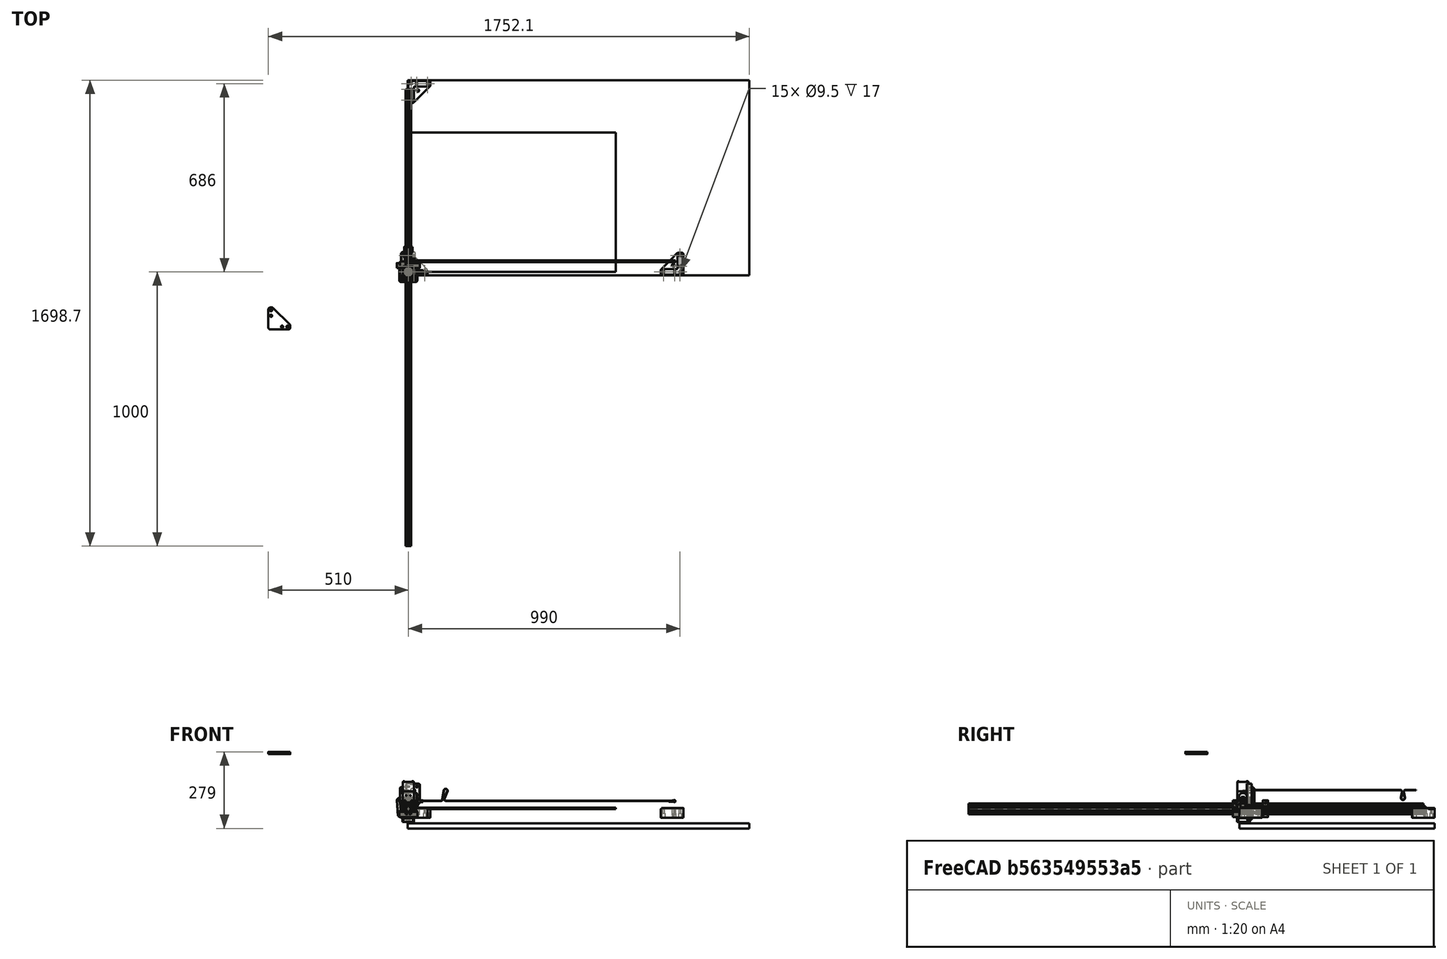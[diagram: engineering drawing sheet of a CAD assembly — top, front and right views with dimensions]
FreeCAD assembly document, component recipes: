
FREECAD ASSEMBLY — COMPONENT RECIPES ("laser-cnc-wf")

This assembly document has 18 components, labeled P0..P17 below (a component is one placed body or linked part). 17 of them carry a construction recipe — the FreeCAD feature program that regenerates the part from scratch, quoted from this document or its linked companion documents; the rest are supplied as boundary geometry only. No exploded tour is included for this assembly.
COMPONENT P0 — recipe-attached ("VSlotBearing", modeled in this document).
Construction recipe (the document's own serialized feature program — sketch geometry with constraints, then the solid features built on it; lengths are millimeters unless a unit is written):

FEATURE [Sketcher::SketchObject] Sketch002  label="BearingProfile"
  FullyConstrained = true
  MapMode = 5
  Placement = pos=(0,0,0) rot=(1,0,0;1.5708rad)
  Support = -> [XZ_Plane001]
  sketch-geometry (9):
    g0: LineSegment StartX=-5.085 StartY=9.91981 StartZ=0 EndX=-5.085 EndY=2.5 EndZ=0
    g1: LineSegment StartX=5.085 StartY=9.91981 StartZ=0 EndX=5.085 EndY=2.5 EndZ=0
    g2: LineSegment StartX=-5.085 StartY=2.5 StartZ=0 EndX=5.085 EndY=2.5 EndZ=0
    g3: LineSegment StartX=-2.98481 StartY=12.02 StartZ=0 EndX=2.98481 EndY=12.02 EndZ=0
    g4: LineSegment StartX=-5.085 StartY=9.91981 StartZ=0 EndX=-2.98481 EndY=12.02 EndZ=0
    g5: LineSegment StartX=2.98481 StartY=12.02 StartZ=0 EndX=5.085 EndY=9.91981 EndZ=0
    g6: GeomPoint X=-7.5024 Y=7.5024 Z=0
    g7: GeomPoint X=7.5024 Y=-7.5024 Z=0
    g8: LineSegment StartX=-7.5024 StartY=7.5024 StartZ=0 EndX=7.5024 EndY=-7.5024 EndZ=0
  constraints (23):
    c: Vertical(g0)
    c: Vertical(g1)
    c: Symmetric(g0,g1,g-2)
    c: DistanceX(g0,g1) = 10.17  'Width'
    c: DistanceY(g-1,g0) = 2.5
    c: Coincident(g2,g0)
    c: Coincident(g2,g1)
    c: Horizontal(g2)
    c: Horizontal(g3)
    c: DistanceY(g3) = 12.02
    c: Coincident(g4,g0)
    c: Coincident(g4,g3)
    c: Coincident(g5,g3)
    c: Coincident(g5,g1)
    c: Angle(g5,g-1) = 0.785398
    c: Perpendicular(g5,g4)
    c: DistanceY(g0) = 9.91981
    c: PointOnObject(g6,g4)
    c: Symmetric(g7,g6,g-1)
    c: Coincident(g8,g6)
    c: Coincident(g8,g7)
    c: Perpendicular(g4,g8)
    c: Distance(g8) = 21.22
FEATURE [PartDesign::Revolution] Revolution
  Angle = 360
  Axis = (1,0,0)
  Base = (0,0,0)
  Placement = pos=(0,0,0) rot=(1,0,0;1.5708rad)
  Profile = -> Sketch002
  ReferenceAxis = -> Sketch002 [H_Axis]
FEATURE [PartDesign::Body] Body  label="VSlotBearing"
  Group = -> [Sketch002,Revolution]
  Origin = -> Origin001
  Tip = -> Revolution
COMPONENT P1 — recipe-attached ("Brace", modeled in this document).
Construction recipe (the document's own serialized feature program — sketch geometry with constraints, then the solid features built on it; lengths are millimeters unless a unit is written):

FEATURE [Sketcher::SketchObject] Sketch006  label="BraceProfile"
  FullyConstrained = true
  MapMode = 5
  Support = -> [XY_Plane009]
  sketch-geometry (20):
    g0: LineSegment StartX=-10 StartY=63 StartZ=0 EndX=-10 EndY=-3 EndZ=0
    g1: LineSegment StartX=-3 StartY=-10 StartZ=0 EndX=63 EndY=-10 EndZ=0
    g2: LineSegment StartX=70 StartY=-3 StartZ=0 EndX=70 EndY=3 EndZ=0
    g3: LineSegment StartX=67.9497 StartY=7.94975 StartZ=0 EndX=7.94975 EndY=67.9497 EndZ=0
    g4: LineSegment StartX=3 StartY=70 StartZ=0 EndX=-3 EndY=70 EndZ=0
    g5: Circle CenterX=40 CenterY=0 CenterZ=0 NormalX=0 NormalY=0 NormalZ=1 AngleXU=0 Radius=4
    g6: Circle CenterX=60 CenterY=0 CenterZ=0 NormalX=0 NormalY=0 NormalZ=1 AngleXU=0 Radius=4
    g7: Circle CenterX=0 CenterY=40 CenterZ=0 NormalX=0 NormalY=0 NormalZ=1 AngleXU=0 Radius=4
    g8: Circle CenterX=0 CenterY=60 CenterZ=0 NormalX=0 NormalY=0 NormalZ=1 AngleXU=0 Radius=4
    g9: LineSegment StartX=10 StartY=100 StartZ=0 EndX=10 EndY=-10 EndZ=0
    g10: LineSegment StartX=10 StartY=-10 StartZ=0 EndX=-10 EndY=-10 EndZ=0
    g11: LineSegment StartX=-10 StartY=-10 StartZ=0 EndX=-10 EndY=100 EndZ=0
    g12: LineSegment StartX=10 StartY=10 StartZ=0 EndX=160 EndY=10 EndZ=0
    g13: LineSegment StartX=160 StartY=-10 StartZ=0 EndX=10 EndY=-10 EndZ=0
    g14: LineSegment StartX=10 StartY=-10 StartZ=0 EndX=10 EndY=10 EndZ=0
    g15: ArcOfCircle CenterX=-3 CenterY=-3 CenterZ=0 NormalX=0 NormalY=0 NormalZ=1 AngleXU=0 Radius=7 StartAngle=3.14159 EndAngle=4.71239
    g16: ArcOfCircle CenterX=-3 CenterY=63 CenterZ=0 NormalX=0 NormalY=0 NormalZ=1 AngleXU=0 Radius=7 StartAngle=1.5708 EndAngle=3.14159
    g17: ArcOfCircle CenterX=3 CenterY=63 CenterZ=0 NormalX=0 NormalY=0 NormalZ=1 AngleXU=0 Radius=7 StartAngle=0.785398 EndAngle=1.5708
    g18: ArcOfCircle CenterX=63 CenterY=3 CenterZ=0 NormalX=0 NormalY=0 NormalZ=1 AngleXU=0 Radius=7 StartAngle=0 EndAngle=0.785398
    g19: ArcOfCircle CenterX=63 CenterY=-3 CenterZ=0 NormalX=0 NormalY=0 NormalZ=1 AngleXU=0 Radius=7 StartAngle=4.71239 EndAngle=6.28319
  constraints (53):
    c: Vertical(g0)
    c: Horizontal(g1)
    c: Vertical(g2)
    c: Horizontal(g4)
    c: PointOnObject(g5,g-1)
    c: PointOnObject(g6,g-1)
    c: PointOnObject(g7,g-2)
    c: PointOnObject(g8,g-2)
    c: Radius(g7) = 4
    c: Equal(g8,g7)
    c: Equal(g7,g5)
    c: Equal(g5,g6)
    c: Distance(g5,g6) = 20
    c: Distance(g7,g8) = 20
    c: Coincident(g9,g10)
    c: Coincident(g10,g11)
    c: Vertical(g9)
    c: Vertical(g11)
    c: DistanceY(g10,g-1) = 10
    c: DistanceX(g10,g10) = 20
    c: Symmetric(g10,g9,g-2)
    c: DistanceY(g11,g11) = 110
    c: Equal(g9,g11)
    c: Coincident(g13,g14)
    c: Coincident(g14,g12)
    c: Horizontal(g12)
    c: Horizontal(g13)
    c: Vertical(g14)
    c: PointOnObject(g13,g10)
    c: DistanceX(g13,g13) = 150
    c: Equal(g13,g12)
    c: Symmetric(g12,g9,g-1)
    c: DistanceX(g-1,g5) = 40
    c: DistanceY(g-1,g7) = 40
    c: Tangent(g0,g15) = -1.5708
    c: Tangent(g1,g15) = -1.5708
    c: Tangent(g0,g16) = -1.5708
    c: Tangent(g4,g16) = -1.5708
    c: Tangent(g4,g17) = -1.5708
    c: Tangent(g3,g17) = -1.5708
    c: Tangent(g3,g18) = -1.5708
    c: Tangent(g2,g18) = -1.5708
    c: Tangent(g2,g19) = -1.5708
    c: Tangent(g1,g19) = -1.5708
    c: Equal(g18,g15)
    c: Equal(g15,g16)
    c: PointOnObject(g0,g11)
    c: Radius(g16) = 7
    c: DistanceY(g8,g4) = 10
    c: PointOnObject(g1,g13)
    c: DistanceX(g6,g2) = 10
    c: Symmetric(g17,g16,g-2)
    c: Symmetric(g18,g19,g-1)
FEATURE [PartDesign::Pad] Pad002
  Direction = (0,0,1)
  Length = 8
  Length2 = 100
  Profile = -> Sketch006
  Type = 0
FEATURE [PartDesign::Body] Body005  label="Brace"
  Group = -> [Sketch006,Pad002]
  Origin = -> Origin009
  Placement = pos=(-500,-200,200) rot=(0,0,1;0rad)
  Tip = -> Pad002
COMPONENT P2 — recipe-attached ("BoltM5_20", modeled in this document).
Construction recipe (the document's own serialized feature program — sketch geometry with constraints, then the solid features built on it; lengths are millimeters unless a unit is written):

FEATURE [Sketcher::SketchObject] Sketch015
  FullyConstrained = true
  MapMode = 5
  Support = -> [XY_Plane014]
  sketch-geometry (6):
    g0: LineSegment StartX=4.17 StartY=5 StartZ=0 EndX=4.17 EndY=0 EndZ=0
    g1: LineSegment StartX=4.17 StartY=0 StartZ=0 EndX=2.45 EndY=0 EndZ=0
    g2: LineSegment StartX=2.45 StartY=0 StartZ=0 EndX=2.45 EndY=-20 EndZ=0
    g3: LineSegment StartX=2.45 StartY=-20 StartZ=0 EndX=0 EndY=-20 EndZ=0
    g4: LineSegment StartX=4.17 StartY=5 StartZ=0 EndX=0 EndY=5 EndZ=0
    g5: LineSegment StartX=0 StartY=5 StartZ=0 EndX=0 EndY=-20 EndZ=0
  constraints (18):
    c: Coincident(g0,g1)
    c: Horizontal(g1)
    c: Vertical(g0)
    c: PointOnObject(g0,g-1)
    c: Coincident(g2,g3)
    c: Horizontal(g3)
    c: Vertical(g2)
    c: Coincident(g2,g1)
    c: PointOnObject(g3,g-2)
    c: Coincident(g4,g0)
    c: PointOnObject(g4,g-2)
    c: Horizontal(g4)
    c: Coincident(g5,g4)
    c: Coincident(g5,g3)
    c: DistanceX(g4,g4) = 4.17
    c: DistanceY(g0,g0) = 5
    c: DistanceY(g2,g2) = 20
    c: DistanceX(g3,g3) = 2.45
FEATURE [PartDesign::Revolution] Revolution001
  Angle = 360
  Axis = (0,1,0)
  Base = (0,0,0)
  Profile = -> Sketch015
  ReferenceAxis = -> Sketch015 [V_Axis]
FEATURE [PartDesign::Body] Body008  label="BoltM5_20"
  Group = -> [Sketch015,Revolution001]
  Origin = -> Origin014
  Tip = -> Revolution001
COMPONENT P3 — recipe-attached ("Stepper47", modeled in this document).
Construction recipe (the document's own serialized feature program — sketch geometry with constraints, then the solid features built on it; lengths are millimeters unless a unit is written):

FEATURE [Sketcher::SketchObject] Sketch017  label="StepperBodyShape"
  FullyConstrained = true
  MapMode = 5
  Support = -> [XY_Plane015]
  sketch-geometry (8):
    g0: LineSegment StartX=-17.1131 StartY=21 StartZ=0 EndX=17.1131 EndY=21 EndZ=0
    g1: LineSegment StartX=21 StartY=17.1131 StartZ=0 EndX=21 EndY=-17.1131 EndZ=0
    g2: LineSegment StartX=17.1131 StartY=-21 StartZ=0 EndX=-17.1131 EndY=-21 EndZ=0
    g3: LineSegment StartX=-21 StartY=-17.1131 StartZ=0 EndX=-21 EndY=17.1131 EndZ=0
    g4: LineSegment StartX=-21 StartY=17.1131 StartZ=0 EndX=-17.1131 EndY=21 EndZ=0
    g5: LineSegment StartX=17.1131 StartY=21 StartZ=0 EndX=21 EndY=17.1131 EndZ=0
    g6: LineSegment StartX=21 StartY=-17.1131 StartZ=0 EndX=17.1131 EndY=-21 EndZ=0
    g7: LineSegment StartX=-21 StartY=-17.1131 StartZ=0 EndX=-17.1131 EndY=-21 EndZ=0
  constraints (24):
    c: Horizontal(g0)
    c: Horizontal(g2)
    c: Vertical(g1)
    c: Vertical(g3)
    c: Coincident(g7,g3)
    c: Coincident(g7,g2)
    c: Coincident(g6,g2)
    c: Coincident(g6,g1)
    c: Coincident(g5,g1)
    c: Coincident(g5,g0)
    c: Coincident(g4,g0)
    c: Coincident(g4,g3)
    c: Angle(g3,g4) = 2.35619
    c: Parallel(g4,g6)
    c: Perpendicular(g4,g7)
    c: Equal(g4,g5)
    c: Equal(g5,g6)
    c: Equal(g6,g7)
    c: Equal(g3,g0)
    c: Equal(g0,g1)
    c: DistanceX(g3,g1) = 42  'Width'
    c: Symmetric(g0,g2,g-1)
    c: Distance(g0,g1) = 53.9
    c: DistanceY(g-1,g0) = 21  'CenterToEdge'
FEATURE [PartDesign::Pad] Pad007  label="StepperBodyPad"
  Direction = (0,0,1)
  Length = 47.9
  Length2 = 100
  Profile = -> Sketch017
  Reversed = true
  Type = 0
FEATURE [Sketcher::SketchObject] Sketch018
  AttachmentOffset = pos=(0,0,21.1) rot=(0,0,1;0rad)
  FullyConstrained = true
  MapMode = 5
  Placement = pos=(0,0,21.1) rot=(0,0,1;0rad)
  Support = -> [XY_Plane015]
  expr: .AttachmentOffset.Base.z = 69mm - Pad007.Length
  sketch-geometry (3):
    g0: ArcOfCircle CenterX=0 CenterY=0 CenterZ=0 NormalX=0 NormalY=0 NormalZ=1 AngleXU=0 Radius=2.5 StartAngle=2.2143 EndAngle=7.21048
    g1: LineSegment StartX=-1.5 StartY=2 StartZ=0 EndX=1.5 EndY=2 EndZ=0
    g2: LineSegment StartX=1.1641e-12 StartY=2 StartZ=0 EndX=-1.6132e-12 EndY=-2.5 EndZ=0
  constraints (10):
    c: Coincident(g0,g-1)
    c: Coincident(g1,g0)
    c: Coincident(g1,g0)
    c: Radius(g0) = 2.5
    c: PointOnObject(g2,g1)
    c: PointOnObject(g2,g0)
    c: Perpendicular(g1,g2)
    c: PointOnObject(g0,g2)
    c: Distance(g2) = 4.5
    c: Horizontal(g1)
FEATURE [Sketcher::SketchObject] Sketch019
  AttachmentOffset = pos=(0,0,7) rot=(0,0,1;0rad)
  FullyConstrained = true
  MapMode = 5
  Placement = pos=(0,0,7) rot=(0,0,1;0rad)
  Support = -> [XY_Plane015]
  sketch-geometry (1):
    g0: Circle CenterX=0 CenterY=0 CenterZ=0 NormalX=0 NormalY=0 NormalZ=1 AngleXU=0 Radius=4
  constraints (2):
    c: Coincident(g0,g-1)
    c: Radius(g0) = 4
FEATURE [Sketcher::SketchObject] Sketch020
  AttachmentOffset = pos=(0,0,6) rot=(0,0,1;0rad)
  FullyConstrained = true
  MapMode = 5
  Placement = pos=(0,0,6) rot=(0,0,1;0rad)
  Support = -> [XY_Plane015]
  sketch-geometry (12):
    g0: ArcOfCircle CenterX=-15.521 CenterY=-15.521 CenterZ=0 NormalX=0 NormalY=0 NormalZ=1 AngleXU=0 Radius=3.87 StartAngle=3.05556 EndAngle=4.79842
    g1: ArcOfCircle CenterX=15.521 CenterY=15.521 CenterZ=0 NormalX=0 NormalY=0 NormalZ=1 AngleXU=0 Radius=3.87 StartAngle=6.19716 EndAngle=7.94001
    g2: ArcOfCircle CenterX=0 CenterY=0 CenterZ=0 NormalX=0 NormalY=0 NormalZ=1 AngleXU=0 Radius=18 StartAngle=1.65682 EndAngle=3.05556
    g3: ArcOfCircle CenterX=0 CenterY=0 CenterZ=0 NormalX=0 NormalY=0 NormalZ=1 AngleXU=0 Radius=18 StartAngle=4.79842 EndAngle=6.19716
    g4: LineSegment StartX=-12.7279 StartY=12.7279 StartZ=0 EndX=12.7279 EndY=-12.7279 EndZ=0
    g5: LineSegment StartX=-17.9334 StartY=1.5466 StartZ=0 EndX=-19.3767 EndY=-15.1885 EndZ=0
    g6: LineSegment StartX=-15.1885 StartY=-19.3767 StartZ=0 EndX=1.5466 EndY=-17.9334 EndZ=0
    g7: LineSegment StartX=17.9334 StartY=-1.5466 StartZ=0 EndX=19.3767 EndY=15.1885 EndZ=0
    g8: LineSegment StartX=15.1885 StartY=19.3767 StartZ=0 EndX=-1.5466 EndY=17.9334 EndZ=0
    g9: Circle CenterX=-15.521 CenterY=-15.521 CenterZ=0 NormalX=0 NormalY=0 NormalZ=1 AngleXU=0 Radius=1.25
    g10: Circle CenterX=15.521 CenterY=15.521 CenterZ=0 NormalX=0 NormalY=0 NormalZ=1 AngleXU=0 Radius=1.25
    g11: LineSegment StartX=-18.2575 StartY=-18.2575 StartZ=0 EndX=18.2575 EndY=18.2575 EndZ=0
  constraints (28):
    c: Coincident(g2,g-1)
    c: Coincident(g3,g2)
    c: PointOnObject(g4,g2)
    c: PointOnObject(g4,g3)
    c: Symmetric(g4,g4,g2)
    c: Distance(g4) = 36
    c: Coincident(g9,g0)
    c: Coincident(g10,g1)
    c: Equal(g10,g9)
    c: Diameter(g9) = 2.5
    c: Distance(g0,g1) = 43.9
    c: Tangent(g5,g2) = -1.5708
    c: Tangent(g8,g2) = -1.5708
    c: Tangent(g8,g1) = -1.5708
    c: Tangent(g7,g1) = -1.5708
    c: Tangent(g7,g3) = -1.5708
    c: Tangent(g6,g3) = -1.5708
    c: Tangent(g6,g0) = -1.5708
    c: Tangent(g5,g0) = -1.5708
    c: Equal(g0,g1)
    c: Symmetric(g0,g1,g2)
    c: PointOnObject(g11,g0)
    c: PointOnObject(g11,g1)
    c: PointOnObject(g2,g11)
    c: Perpendicular(g11,g4)
    c: Distance(g11) = 51.64
    c: Angle(g11,g-1) = 2.35619
    c: PointOnObject(g0,g11)
FEATURE [Sketcher::SketchObject] Sketch021
  FullyConstrained = true
  MapMode = 5
  Support = -> [XY_Plane015]
  sketch-geometry (1):
    g0: Circle CenterX=0 CenterY=0 CenterZ=0 NormalX=0 NormalY=0 NormalZ=1 AngleXU=0 Radius=17
  constraints (2):
    c: Coincident(g0,g-1)
    c: Diameter(g0) = 34
FEATURE [PartDesign::Pad] Pad010
  BaseFeature = -> Pad007
  Direction = (0,0,1)
  Length = 5
  Length2 = 100
  Profile = -> Sketch021
  Type = 0
FEATURE [PartDesign::Pad] Pad009
  BaseFeature = -> Pad010
  Direction = (0,0,1)
  Length = 1
  Length2 = 100
  Profile = -> Sketch020
  Reversed = true
  Type = 0
FEATURE [PartDesign::Pocket] Pocket006
  BaseFeature = -> Pad009
  Length = 10
  Length2 = 100
  Profile = -> Sketch019
  Type = 0
FEATURE [PartDesign::Pad] Pad008
  BaseFeature = -> Pocket006
  Direction = (0,0,-1)
  Length = 10
  Length2 = 100
  Profile = -> Sketch018
  Type = 2
  UseCustomVector = true
FEATURE [Sketcher::SketchObject] Sketch022
  AttachmentOffset = pos=(0,0,-47.9) rot=(0,0,1;0rad)
  FullyConstrained = true
  MapMode = 5
  Placement = pos=(0,0,-47.9) rot=(0,0,1;0rad)
  Support = -> [XY_Plane015]
  expr: .AttachmentOffset.Base.z = -<<StepperBodyPad>>.Length
  expr: Constraints[10] = <<StepperBodyShape>>.Constraints.CenterToEdge
  sketch-geometry (4):
    g0: LineSegment StartX=-8.1 StartY=25 StartZ=0 EndX=8.1 EndY=25 EndZ=0
    g1: LineSegment StartX=8.1 StartY=25 StartZ=0 EndX=8.1 EndY=21 EndZ=0
    g2: LineSegment StartX=8.1 StartY=21 StartZ=0 EndX=-8.1 EndY=21 EndZ=0
    g3: LineSegment StartX=-8.1 StartY=21 StartZ=0 EndX=-8.1 EndY=25 EndZ=0
  constraints (11):
    c: Coincident(g0,g1)
    c: Coincident(g1,g2)
    c: Coincident(g2,g3)
    c: Coincident(g3,g0)
    c: Horizontal(g2)
    c: Vertical(g1)
    c: Vertical(g3)
    c: DistanceX(g0,g0) = 16.2
    c: Symmetric(g0,g0,g-2)
    c: DistanceY(g3,g3) = 4
    c: DistanceY(g-1,g2) = 21
FEATURE [PartDesign::Pad] Pad011
  BaseFeature = -> Pad008
  Direction = (0,0,1)
  Length = 10.25
  Length2 = 100
  Profile = -> Sketch022
  Type = 0
FEATURE [PartDesign::Body] Body009  label="Stepper47"
  Group = -> [Sketch017,Pad007,Sketch018,Sketch019,Sketch020,Sketch021,Pad010,Pad009,Pocket006,Pad008,Sketch022,Pad011]
  Origin = -> Origin015
  Tip = -> Pad011
COMPONENT P4 — recipe-attached ("GT2Pulley5mm", modeled in this document).
Construction recipe (the document's own serialized feature program — sketch geometry with constraints, then the solid features built on it; lengths are millimeters unless a unit is written):

FEATURE [Sketcher::SketchObject] Sketch023  label="GT2Pully5mmProfile"
  FullyConstrained = true
  MapMode = 5
  Placement = pos=(0,0,0) rot=(1,0,0;1.5708rad)
  Support = -> [XZ_Plane016]
  sketch-geometry (9):
    g0: LineSegment StartX=6 StartY=-3.57 StartZ=0 EndX=8 EndY=-3.57 EndZ=0
    g1: LineSegment StartX=8 StartY=-3.57 StartZ=0 EndX=8 EndY=-11.07 EndZ=0
    g2: LineSegment StartX=8 StartY=-11.07 StartZ=0 EndX=2.5 EndY=-11.07 EndZ=0
    g3: LineSegment StartX=2.5 StartY=-11.07 StartZ=0 EndX=2.5 EndY=4.87 EndZ=0
    g4: LineSegment StartX=2.5 StartY=4.87 StartZ=0 EndX=8 EndY=4.87 EndZ=0
    g5: LineSegment StartX=8 StartY=4.87 StartZ=0 EndX=8 EndY=3.57 EndZ=0
    g6: LineSegment StartX=8 StartY=3.57 StartZ=0 EndX=6 EndY=3.57 EndZ=0
    g7: LineSegment StartX=6 StartY=3.57 StartZ=0 EndX=6 EndY=-3.57 EndZ=0
    g8: GeomPoint X=6 Y=0 Z=0
  constraints (25):
    c: Horizontal(g0)
    c: Coincident(g0,g1)
    c: Vertical(g1)
    c: Coincident(g1,g2)
    c: Horizontal(g2)
    c: Coincident(g2,g3)
    c: Vertical(g3)
    c: Coincident(g3,g4)
    c: Horizontal(g4)
    c: Coincident(g4,g5)
    c: Coincident(g5,g6)
    c: Horizontal(g6)
    c: Coincident(g6,g7)
    c: Coincident(g7,g0)
    c: Vertical(g7)
    c: PointOnObject(g4,g1)
    c: DistanceX(g6) = 6
    c: DistanceX(g1) = 8
    c: Vertical(g5)
    c: DistanceY(g0,g5) = 7.14
    c: DistanceY(g5,g5) = 1.3
    c: DistanceY(g1,g1) = 7.5
    c: DistanceX(g2) = 2.5
    c: Symmetric(g0,g6,g8)
    c: PointOnObject(g8,g-1)
FEATURE [PartDesign::Revolution] Revolution002
  Angle = 360
  Axis = (0,-2e-16,1)
  Base = (0,0,0)
  Placement = pos=(0,0,0) rot=(1,0,0;1.5708rad)
  Profile = -> Sketch023
  ReferenceAxis = -> Sketch023 [V_Axis]
  Reversed = true
FEATURE [PartDesign::Body] Body010  label="GT2Pulley5mm"
  Group = -> [Sketch023,Revolution002]
  Origin = -> Origin016
  Tip = -> Revolution002
COMPONENT P5 — recipe-attached ("GT2Idler5mm", modeled in this document).
Construction recipe (the document's own serialized feature program — sketch geometry with constraints, then the solid features built on it; lengths are millimeters unless a unit is written):

FEATURE [Sketcher::SketchObject] Sketch027  label="GT2Idler5mmProfile"
  FullyConstrained = true
  MapMode = 5
  Placement = pos=(0,0,0) rot=(1,0,0;1.5708rad)
  Support = -> [XZ_Plane018]
  sketch-geometry (9):
    g0: LineSegment StartX=8.95 StartY=-3.25 StartZ=0 EndX=8.95 EndY=-4.25 EndZ=0
    g1: LineSegment StartX=8.95 StartY=-4.25 StartZ=0 EndX=2.5 EndY=-4.25 EndZ=0
    g2: LineSegment StartX=2.5 StartY=-4.25 StartZ=0 EndX=2.5 EndY=4.25 EndZ=0
    g3: LineSegment StartX=2.5 StartY=4.25 StartZ=0 EndX=8.95 EndY=4.25 EndZ=0
    g4: LineSegment StartX=8.95 StartY=4.25 StartZ=0 EndX=8.95 EndY=3.25 EndZ=0
    g5: LineSegment StartX=8.95 StartY=3.25 StartZ=0 EndX=6 EndY=3.25 EndZ=0
    g6: LineSegment StartX=8.95 StartY=-3.25 StartZ=0 EndX=6 EndY=-3.25 EndZ=0
    g7: LineSegment StartX=6 StartY=-3.25 StartZ=0 EndX=6 EndY=3.25 EndZ=0
    g8: GeomPoint X=6 Y=0 Z=0
  constraints (26):
    c: Vertical(g0)
    c: Coincident(g0,g1)
    c: Horizontal(g1)
    c: Coincident(g1,g2)
    c: Vertical(g2)
    c: Coincident(g2,g3)
    c: Horizontal(g3)
    c: Coincident(g3,g4)
    c: Coincident(g4,g5)
    c: Horizontal(g5)
    c: PointOnObject(g3,g0)
    c: DistanceX(g5) = 6  'Radius'
    c: DistanceX(g0) = 8.95  'RimRadius'
    c: Vertical(g4)
    c: DistanceY(g4,g4) = 1
    c: DistanceY(g0,g0) = 1
    c: DistanceX(g1) = 2.5
    c: Coincident(g6,g0)
    c: Horizontal(g6)
    c: Coincident(g7,g6)
    c: Coincident(g7,g5)
    c: Vertical(g7)
    c: Symmetric(g5,g6,g8)
    c: DistanceY(g7,g7) = 6.5
    c: PointOnObject(g8,g-1)
    c: DistanceY(g2,g2) = 8.5  'Height'
FEATURE [PartDesign::Revolution] Revolution003
  Angle = 360
  Axis = (0,-2e-16,1)
  Base = (0,0,0)
  Placement = pos=(0,0,0) rot=(1,0,0;1.5708rad)
  Profile = -> Sketch027
  ReferenceAxis = -> Sketch027 [V_Axis]
  Reversed = true
FEATURE [PartDesign::Body] Body011  label="GT2Idler5mm"
  Group = -> [Sketch027,Revolution003]
  Origin = -> Origin018
  Tip = -> Revolution003
COMPONENT P6 — recipe-attached ("NutM5Square", modeled in this document).
Construction recipe (the document's own serialized feature program — sketch geometry with constraints, then the solid features built on it; lengths are millimeters unless a unit is written):

FEATURE [Sketcher::SketchObject] Sketch029
  FullyConstrained = true
  MapMode = 5
  Support = -> [XY_Plane021]
  sketch-geometry (9):
    g0: LineSegment StartX=-3.51 StartY=3.91 StartZ=0 EndX=3.51 EndY=3.91 EndZ=0
    g1: LineSegment StartX=3.91 StartY=3.51 StartZ=0 EndX=3.91 EndY=-3.51 EndZ=0
    g2: LineSegment StartX=3.51 StartY=-3.91 StartZ=0 EndX=-3.51 EndY=-3.91 EndZ=0
    g3: LineSegment StartX=-3.91 StartY=-3.51 StartZ=0 EndX=-3.91 EndY=3.51 EndZ=0
    g4: Circle CenterX=0 CenterY=0 CenterZ=0 NormalX=0 NormalY=0 NormalZ=1 AngleXU=0 Radius=2.22
    g5: ArcOfCircle CenterX=-3.51 CenterY=3.51 CenterZ=0 NormalX=0 NormalY=0 NormalZ=1 AngleXU=0 Radius=0.4 StartAngle=1.5708 EndAngle=3.14159
    g6: ArcOfCircle CenterX=3.51 CenterY=3.51 CenterZ=0 NormalX=0 NormalY=0 NormalZ=1 AngleXU=0 Radius=0.4 StartAngle=0 EndAngle=1.5708
    g7: ArcOfCircle CenterX=3.51 CenterY=-3.51 CenterZ=0 NormalX=0 NormalY=0 NormalZ=1 AngleXU=0 Radius=0.4 StartAngle=4.71239 EndAngle=6.28319
    g8: ArcOfCircle CenterX=-3.51 CenterY=-3.51 CenterZ=0 NormalX=0 NormalY=0 NormalZ=1 AngleXU=0 Radius=0.4 StartAngle=3.14159 EndAngle=4.71239
  constraints (21):
    c: Horizontal(g0)
    c: Horizontal(g2)
    c: Vertical(g1)
    c: Vertical(g3)
    c: Equal(g3,g0)
    c: Coincident(g4,g-1)
    c: Diameter(g4) = 4.44
    c: Tangent(g3,g5) = 1.5708
    c: Tangent(g0,g5) = 1.5708
    c: Tangent(g0,g6) = 1.5708
    c: Tangent(g1,g6) = 1.5708
    c: Tangent(g1,g7) = 1.5708
    c: Tangent(g2,g7) = 1.5708
    c: Tangent(g2,g8) = 1.5708
    c: Tangent(g3,g8) = 1.5708
    c: Equal(g5,g6)
    c: Equal(g6,g7)
    c: Equal(g7,g8)
    c: Radius(g5) = 0.4
    c: DistanceX(g3,g1) = 7.82
    c: Symmetric(g5,g7,g4)
FEATURE [PartDesign::Pad] Pad012
  Direction = (0,0,1)
  Length = 3.62
  Length2 = 100
  Profile = -> Sketch029
  Type = 0
FEATURE [PartDesign::Body] Body013  label="NutM5Square"
  Group = -> [Sketch029,Pad012]
  Origin = -> Origin021
  Tip = -> Pad012
COMPONENT P7 — recipe-attached ("BoltM5_30", modeled in this document).
Construction recipe (the document's own serialized feature program — sketch geometry with constraints, then the solid features built on it; lengths are millimeters unless a unit is written):

FEATURE [Sketcher::SketchObject] Sketch031
  FullyConstrained = true
  MapMode = 5
  sketch-geometry (6):
    g0: LineSegment StartX=4.17 StartY=5 StartZ=0 EndX=4.17 EndY=0 EndZ=0
    g1: LineSegment StartX=4.17 StartY=0 StartZ=0 EndX=2.45 EndY=0 EndZ=0
    g2: LineSegment StartX=2.45 StartY=0 StartZ=0 EndX=2.45 EndY=-30 EndZ=0
    g3: LineSegment StartX=2.45 StartY=-30 StartZ=0 EndX=0 EndY=-30 EndZ=0
    g4: LineSegment StartX=4.17 StartY=5 StartZ=0 EndX=0 EndY=5 EndZ=0
    g5: LineSegment StartX=0 StartY=5 StartZ=0 EndX=0 EndY=-30 EndZ=0
  constraints (18):
    c: Coincident(g0,g1)
    c: Horizontal(g1)
    c: Vertical(g0)
    c: PointOnObject(g0,g-1)
    c: Coincident(g2,g3)
    c: Horizontal(g3)
    c: Vertical(g2)
    c: Coincident(g2,g1)
    c: PointOnObject(g3,g-2)
    c: Coincident(g4,g0)
    c: PointOnObject(g4,g-2)
    c: Horizontal(g4)
    c: Coincident(g5,g4)
    c: Coincident(g5,g3)
    c: DistanceX(g4,g4) = 4.17
    c: DistanceY(g0,g0) = 5
    c: DistanceY(g2,g2) = 30
    c: DistanceX(g3,g3) = 2.45
FEATURE [PartDesign::Revolution] Revolution005
  Angle = 360
  Axis = (0,1,0)
  Base = (0,0,0)
  Profile = -> Sketch031
  ReferenceAxis = -> Sketch031 [V_Axis]
FEATURE [PartDesign::Body] Body014  label="BoltM5_30"
  Group = -> [Sketch031,Revolution005]
  Origin = -> Origin022
  Tip = -> Revolution005
COMPONENT P8 — recipe-attached ("BoltM5_35", modeled in this document).
Construction recipe (the document's own serialized feature program — sketch geometry with constraints, then the solid features built on it; lengths are millimeters unless a unit is written):

FEATURE [Sketcher::SketchObject] Sketch032
  FullyConstrained = true
  MapMode = 5
  sketch-geometry (6):
    g0: LineSegment StartX=4.17 StartY=5 StartZ=0 EndX=4.17 EndY=0 EndZ=0
    g1: LineSegment StartX=4.17 StartY=0 StartZ=0 EndX=2.45 EndY=0 EndZ=0
    g2: LineSegment StartX=2.45 StartY=0 StartZ=0 EndX=2.45 EndY=-35 EndZ=0
    g3: LineSegment StartX=2.45 StartY=-35 StartZ=0 EndX=0 EndY=-35 EndZ=0
    g4: LineSegment StartX=4.17 StartY=5 StartZ=0 EndX=0 EndY=5 EndZ=0
    g5: LineSegment StartX=0 StartY=5 StartZ=0 EndX=0 EndY=-35 EndZ=0
  constraints (18):
    c: Coincident(g0,g1)
    c: Horizontal(g1)
    c: Vertical(g0)
    c: PointOnObject(g0,g-1)
    c: Coincident(g2,g3)
    c: Horizontal(g3)
    c: Vertical(g2)
    c: Coincident(g2,g1)
    c: PointOnObject(g3,g-2)
    c: Coincident(g4,g0)
    c: PointOnObject(g4,g-2)
    c: Horizontal(g4)
    c: Coincident(g5,g4)
    c: Coincident(g5,g3)
    c: DistanceX(g4,g4) = 4.17
    c: DistanceY(g0,g0) = 5
    c: DistanceY(g2,g2) = 35
    c: DistanceX(g3,g3) = 2.45
FEATURE [PartDesign::Revolution] Revolution006
  Angle = 360
  Axis = (0,1,0)
  Base = (0,0,0)
  Profile = -> Sketch032
  ReferenceAxis = -> Sketch032 [V_Axis]
FEATURE [PartDesign::Body] Body015  label="BoltM5_35"
  Group = -> [Sketch032,Revolution006]
  Origin = -> Origin023
  Tip = -> Revolution006
COMPONENT P9 — recipe-attached ("BeltAdjustHook", modeled in this document).
Construction recipe (the document's own serialized feature program — sketch geometry with constraints, then the solid features built on it; lengths are millimeters unless a unit is written):

FEATURE [Sketcher::SketchObject] Sketch054
  AttachmentOffset = pos=(0,28.35,-20) rot=(0,0,1;0rad)
  FullyConstrained = true
  MapMode = 5
  Placement = pos=(20,1.9e-15,28.35) rot=(-0.57735,0.57735,0.57735;4.18879rad)
  Support = -> [YZ_Plane030]
  expr: .AttachmentOffset.Base.y = 28.35
  sketch-geometry (8):
    g0: LineSegment StartX=-0.353553 StartY=6.71751 StartZ=0 EndX=-6.71751 EndY=0.353553 EndZ=0
    g1: LineSegment StartX=-0.353553 StartY=-6.71751 StartZ=0 EndX=-6.71751 EndY=-0.353553 EndZ=0
    g2: LineSegment StartX=0.353553 StartY=6.71751 StartZ=0 EndX=6.71751 EndY=0.353553 EndZ=0
    g3: LineSegment StartX=6.71751 StartY=-0.353553 StartZ=0 EndX=0.353553 EndY=-6.71751 EndZ=0
    g4: ArcOfCircle CenterX=1.3e-15 CenterY=6.36396 CenterZ=0 NormalX=0 NormalY=0 NormalZ=1 AngleXU=0 Radius=0.5 StartAngle=0.785398 EndAngle=2.35619
    g5: ArcOfCircle CenterX=6.36396 CenterY=0 CenterZ=0 NormalX=0 NormalY=0 NormalZ=1 AngleXU=0 Radius=0.5 StartAngle=5.49779 EndAngle=7.06858
    g6: ArcOfCircle CenterX=-1.3e-15 CenterY=-6.36396 CenterZ=0 NormalX=0 NormalY=0 NormalZ=1 AngleXU=0 Radius=0.5 StartAngle=3.92699 EndAngle=5.49779
    g7: ArcOfCircle CenterX=-6.36396 CenterY=1e-16 CenterZ=0 NormalX=0 NormalY=0 NormalZ=1 AngleXU=0 Radius=0.5 StartAngle=2.35619 EndAngle=3.92699
  constraints (19):
    c: Parallel(g2,g1)
    c: Parallel(g0,g3)
    c: Perpendicular(g3,g2)
    c: Tangent(g0,g4) = -1.5708
    c: Tangent(g2,g4) = 1.5708
    c: Tangent(g2,g5) = 1.5708
    c: Tangent(g3,g5) = 1.5708
    c: Tangent(g3,g6) = 1.5708
    c: Tangent(g1,g6) = 1.5708
    c: Tangent(g1,g7) = 1.5708
    c: Tangent(g0,g7) = -1.5708
    c: Equal(g4,g5)
    c: Equal(g5,g6)
    c: Equal(g6,g7)
    c: Distance(g0,g3) = 10
    c: Equal(g0,g2)
    c: Radius(g4) = 0.5
    c: Symmetric(g4,g6,g-1)
    c: PointOnObject(g5,g-1)
FEATURE [Sketcher::SketchObject] Sketch056
  AttachmentOffset = pos=(47,28.35,0) rot=(0,0,1;0rad)
  FullyConstrained = false
  MapMode = 5
  Placement = pos=(47,-6.3e-15,28.35) rot=(1,0,0;1.5708rad)
  Support = -> [XZ_Plane030]
  expr: .AttachmentOffset.Base.y = 28.35
  sketch-geometry (7):
    g0: ArcOfCircle CenterX=0 CenterY=0 CenterZ=0 NormalX=0 NormalY=0 NormalZ=1 AngleXU=0 Radius=3.25413 StartAngle=1.30814 EndAngle=4.97505
    g1: LineSegment StartX=0.844932 StartY=-3.14252 StartZ=0 EndX=12.5328 EndY=-9e-16 EndZ=0
    g2: LineSegment StartX=0.844932 StartY=3.14252 StartZ=0 EndX=12.5328 EndY=-9e-16 EndZ=0
    g3: LineSegment StartX=20.145 StartY=2 StartZ=0 EndX=1.85962 EndY=6.91642 EndZ=0
    g4: LineSegment StartX=20.145 StartY=-2 StartZ=0 EndX=1.85962 EndY=-6.91642 EndZ=0
    g5: ArcOfCircle CenterX=0 CenterY=0 CenterZ=0 NormalX=0 NormalY=0 NormalZ=1 AngleXU=0 Radius=7.16205 StartAngle=1.30814 EndAngle=4.97505
    g6: LineSegment StartX=20.145 StartY=2 StartZ=0 EndX=20.145 EndY=-2 EndZ=0
  constraints (14):
    c: Coincident(g0,g-1)
    c: Coincident(g2,g1)
    c: PointOnObject(g1,g-1)
    c: Tangent(g2,g0) = 1.5708
    c: Tangent(g1,g0) = -1.5708
    c: Coincident(g5,g0)
    c: Coincident(g6,g3)
    c: Coincident(g6,g4)
    c: Vertical(g6)
    c: Parallel(g3,g2)
    c: Parallel(g1,g4)
    c: DistanceY(g6,g6) = 4
    c: Tangent(g5,g4) = 1.5708
    c: Tangent(g5,g3) = -1.5708
FEATURE [Sketcher::SketchObject] Sketch057
  AttachmentOffset = pos=(0,28.35,-20) rot=(0,0,1;0rad)
  FullyConstrained = true
  MapMode = 5
  Placement = pos=(20,1.9e-15,28.35) rot=(-0.57735,0.57735,0.57735;4.18879rad)
  Support = -> [YZ_Plane030]
  expr: .AttachmentOffset.Base.y = 28.35
  sketch-geometry (1):
    g0: Circle CenterX=0 CenterY=0 CenterZ=0 NormalX=0 NormalY=0 NormalZ=1 AngleXU=0 Radius=2.15
  constraints (2):
    c: Coincident(g0,g-1)
    c: Diameter(g0) = 4.3
FEATURE [PartDesign::Pad] Pad023
  Direction = (-1,2e-16,-3e-16)
  Length = 34
  Length2 = 100
  Placement = pos=(0,0,0) rot=(0.57735,0.57735,0.57735;2.0944rad)
  Profile = -> Sketch054
  Reversed = true
  Type = 0
FEATURE [Sketcher::SketchObject] Sketch067
  AttachmentOffset = pos=(47,28.35,0) rot=(0,0,1;0rad)
  FullyConstrained = false
  MapMode = 5
  Placement = pos=(47,-6.3e-15,28.35) rot=(1,0,0;1.5708rad)
  Support = -> [XZ_Plane030]
  expr: .AttachmentOffset.Base.y = 28.35
  sketch-geometry (8):
    g0: LineSegment StartX=-10.8854 StartY=12.5794 StartZ=0 EndX=24.1708 EndY=12.5794 EndZ=0
    g1: LineSegment StartX=24.1708 StartY=12.5794 StartZ=0 EndX=24.1708 EndY=4.19188 EndZ=0
    g2: LineSegment StartX=24.1708 StartY=4.19188 StartZ=0 EndX=-3.02777 EndY=4.19188 EndZ=0
    g3: LineSegment StartX=-3.02777 StartY=4.19188 StartZ=0 EndX=-10.8854 EndY=12.5794 EndZ=0
    g4: LineSegment StartX=24.1708 StartY=-4.19188 StartZ=0 EndX=-3.02777 EndY=-4.19188 EndZ=0
    g5: LineSegment StartX=-3.02777 StartY=-4.19188 StartZ=0 EndX=-11.5804 EndY=-12.5794 EndZ=0
    g6: LineSegment StartX=-11.5804 StartY=-12.5794 StartZ=0 EndX=24.1708 EndY=-12.5794 EndZ=0
    g7: LineSegment StartX=24.1708 StartY=-12.5794 StartZ=0 EndX=24.1708 EndY=-4.19188 EndZ=0
  constraints (15):
    c: Coincident(g0,g1)
    c: Coincident(g1,g2)
    c: Coincident(g2,g3)
    c: Coincident(g3,g0)
    c: Horizontal(g0)
    c: Vertical(g1)
    c: Coincident(g4,g5)
    c: Coincident(g5,g6)
    c: Coincident(g6,g7)
    c: Coincident(g7,g4)
    c: Horizontal(g4)
    c: Horizontal(g6)
    c: Vertical(g2,g4)
    c: Symmetric(g1,g4,g-1)
    c: Symmetric(g0,g6,g-1)
FEATURE [PartDesign::Pocket] Pocket032
  BaseFeature = -> Pad023
  Length = 5
  Length2 = 100
  Midplane = true
  Placement = pos=(0,0,0) rot=(0.57735,0.57735,0.57735;2.0944rad)
  Profile = -> Sketch067
  Type = 1
FEATURE [PartDesign::Pocket] Pocket033
  BaseFeature = -> Pocket032
  Length = 7
  Length2 = 100
  Midplane = true
  Placement = pos=(0,0,0) rot=(0.57735,0.57735,0.57735;2.0944rad)
  Profile = -> Sketch056
  Type = 0
FEATURE [PartDesign::Pocket] Pocket034
  BaseFeature = -> Pocket033
  Length = 21
  Length2 = 100
  Placement = pos=(0,0,0) rot=(0.57735,0.57735,0.57735;2.0944rad)
  Profile = -> Sketch057
  Type = 0
FEATURE [Sketcher::SketchObject] Sketch068
  AttachmentOffset = pos=(0,28.35,-23) rot=(0,0,1;0.785398rad)
  FullyConstrained = true
  MapMode = 5
  Placement = pos=(23,1.2e-15,28.35) rot=(-0.357407,0.862856,0.357407;4.56541rad)
  Support = -> [YZ_Plane030]
  expr: .AttachmentOffset.Base.y = 28.35
  sketch-geometry (7):
    g0: LineSegment StartX=-3.65 StartY=-3.65 StartZ=0 EndX=3.65 EndY=-3.65 EndZ=0
    g1: LineSegment StartX=3.65 StartY=-3.65 StartZ=0 EndX=3.65 EndY=3.65 EndZ=0
    g2: LineSegment StartX=3.65 StartY=3.65 StartZ=0 EndX=-3.65 EndY=3.65 EndZ=0
    g3: LineSegment StartX=-3.65 StartY=3.65 StartZ=0 EndX=-3.65 EndY=-3.65 EndZ=0
    g4: LineSegment StartX=-3.65 StartY=3.65 StartZ=0 EndX=-4.4 EndY=8.65 EndZ=0
    g5: LineSegment StartX=-4.4 StartY=8.65 StartZ=0 EndX=4.4 EndY=8.65 EndZ=0
    g6: LineSegment StartX=4.4 StartY=8.65 StartZ=0 EndX=3.65 EndY=3.65 EndZ=0
  constraints (18):
    c: Coincident(g0,g1)
    c: Coincident(g1,g2)
    c: Coincident(g2,g3)
    c: Coincident(g3,g0)
    c: Horizontal(g0)
    c: Horizontal(g2)
    c: Vertical(g1)
    c: Vertical(g3)
    c: DistanceX(g2,g2) = 7.3
    c: Equal(g2,g3)
    c: Symmetric(g2,g0,g-1)
    c: Coincident(g4,g3)
    c: Coincident(g5,g4)
    c: Coincident(g6,g5)
    c: Coincident(g6,g1)
    c: Symmetric(g4,g5,g-2)
    c: DistanceX(g5,g5) = 8.8
    c: DistanceY(g3,g4) = 5
FEATURE [PartDesign::Pocket] Pocket035
  BaseFeature = -> Pocket034
  Length = 3.5
  Length2 = 100
  Placement = pos=(0,0,0) rot=(0.57735,0.57735,0.57735;2.0944rad)
  Profile = -> Sketch068
  Type = 0
FEATURE [Sketcher::SketchObject] Sketch069
  AttachmentOffset = pos=(0,28.35,-20) rot=(0,0,1;0rad)
  FullyConstrained = true
  MapMode = 5
  Placement = pos=(20,1.9e-15,28.35) rot=(-0.57735,0.57735,0.57735;4.18879rad)
  Support = -> [YZ_Plane030]
  expr: .AttachmentOffset.Base.y = 28.35
  sketch-geometry (1):
    g0: Circle CenterX=0 CenterY=0 CenterZ=0 NormalX=0 NormalY=0 NormalZ=1 AngleXU=0 Radius=3.15
  constraints (2):
    c: Coincident(g0,g-1)
    c: Diameter(g0) = 6.3
FEATURE [PartDesign::Pocket] Pocket036
  BaseFeature = -> Pocket035
  Length = 4
  Length2 = 100
  Placement = pos=(0,0,0) rot=(0.57735,0.57735,0.57735;2.0944rad)
  Profile = -> Sketch069
  Type = 0
FEATURE [PartDesign::Body] Body020  label="BeltAdjustHook"
  Group = -> [Sketch054,Sketch056,Sketch057,Pad023,Sketch067,Pocket032,Pocket033,Pocket034,Sketch068,Pocket035,Sketch069,Pocket036]
  Origin = -> Origin030
  Tip = -> Pocket036
COMPONENT P10 — recipe-attached ("Stepper34", modeled in this document).
Construction recipe (the document's own serialized feature program — sketch geometry with constraints, then the solid features built on it; lengths are millimeters unless a unit is written):

FEATURE [Sketcher::SketchObject] Sketch059  label="StepperBodyShape001"
  FullyConstrained = true
  MapMode = 5
  Support = -> [XY_Plane031]
  sketch-geometry (8):
    g0: LineSegment StartX=-17.1131 StartY=21 StartZ=0 EndX=17.1131 EndY=21 EndZ=0
    g1: LineSegment StartX=21 StartY=17.1131 StartZ=0 EndX=21 EndY=-17.1131 EndZ=0
    g2: LineSegment StartX=17.1131 StartY=-21 StartZ=0 EndX=-17.1131 EndY=-21 EndZ=0
    g3: LineSegment StartX=-21 StartY=-17.1131 StartZ=0 EndX=-21 EndY=17.1131 EndZ=0
    g4: LineSegment StartX=-21 StartY=17.1131 StartZ=0 EndX=-17.1131 EndY=21 EndZ=0
    g5: LineSegment StartX=17.1131 StartY=21 StartZ=0 EndX=21 EndY=17.1131 EndZ=0
    g6: LineSegment StartX=21 StartY=-17.1131 StartZ=0 EndX=17.1131 EndY=-21 EndZ=0
    g7: LineSegment StartX=-21 StartY=-17.1131 StartZ=0 EndX=-17.1131 EndY=-21 EndZ=0
  constraints (24):
    c: Horizontal(g0)
    c: Horizontal(g2)
    c: Vertical(g1)
    c: Vertical(g3)
    c: Coincident(g7,g3)
    c: Coincident(g7,g2)
    c: Coincident(g6,g2)
    c: Coincident(g6,g1)
    c: Coincident(g5,g1)
    c: Coincident(g5,g0)
    c: Coincident(g4,g0)
    c: Coincident(g4,g3)
    c: Angle(g3,g4) = 2.35619
    c: Parallel(g4,g6)
    c: Perpendicular(g4,g7)
    c: Equal(g4,g5)
    c: Equal(g5,g6)
    c: Equal(g6,g7)
    c: Equal(g3,g0)
    c: Equal(g0,g1)
    c: DistanceX(g3,g1) = 42
    c: Symmetric(g0,g2,g-1)
    c: Distance(g0,g1) = 53.9
    c: DistanceY(g-1,g0) = 21  'CenterToEdge'
FEATURE [PartDesign::Pad] Pad017  label="StepperBodyPad001"
  Direction = (0,0,1)
  Length = 33.9
  Length2 = 100
  Profile = -> Sketch059
  Reversed = true
  Type = 0
FEATURE [Sketcher::SketchObject] Sketch060
  AttachmentOffset = pos=(0,0,20.1) rot=(0,0,1;0rad)
  FullyConstrained = true
  MapMode = 5
  Placement = pos=(0,0,20.1) rot=(0,0,1;0rad)
  Support = -> [XY_Plane031]
  expr: .AttachmentOffset.Base.z = 54mm - Pad017.Length
  sketch-geometry (3):
    g0: ArcOfCircle CenterX=0 CenterY=0 CenterZ=0 NormalX=0 NormalY=0 NormalZ=1 AngleXU=0 Radius=2.5 StartAngle=2.2143 EndAngle=7.21048
    g1: LineSegment StartX=-1.5 StartY=2 StartZ=0 EndX=1.5 EndY=2 EndZ=0
    g2: LineSegment StartX=1.1641e-12 StartY=2 StartZ=0 EndX=-1.6132e-12 EndY=-2.5 EndZ=0
  constraints (10):
    c: Coincident(g0,g-1)
    c: Coincident(g1,g0)
    c: Coincident(g1,g0)
    c: Radius(g0) = 2.5
    c: PointOnObject(g2,g1)
    c: PointOnObject(g2,g0)
    c: Perpendicular(g1,g2)
    c: PointOnObject(g0,g2)
    c: Distance(g2) = 4.5
    c: Horizontal(g1)
FEATURE [Sketcher::SketchObject] Sketch061
  AttachmentOffset = pos=(0,0,7) rot=(0,0,1;0rad)
  FullyConstrained = true
  MapMode = 5
  Placement = pos=(0,0,7) rot=(0,0,1;0rad)
  Support = -> [XY_Plane031]
  sketch-geometry (1):
    g0: Circle CenterX=0 CenterY=0 CenterZ=0 NormalX=0 NormalY=0 NormalZ=1 AngleXU=0 Radius=4
  constraints (2):
    c: Coincident(g0,g-1)
    c: Radius(g0) = 4
FEATURE [Sketcher::SketchObject] Sketch063
  FullyConstrained = true
  MapMode = 5
  Support = -> [XY_Plane031]
  sketch-geometry (1):
    g0: Circle CenterX=0 CenterY=0 CenterZ=0 NormalX=0 NormalY=0 NormalZ=1 AngleXU=0 Radius=11
  constraints (2):
    c: Coincident(g0,g-1)
    c: Diameter(g0) = 22
FEATURE [PartDesign::Pad] Pad020
  BaseFeature = -> Pad017
  Direction = (0,0,1)
  Length = 2
  Length2 = 100
  Profile = -> Sketch063
  Type = 0
FEATURE [PartDesign::Pocket] Pocket030
  BaseFeature = -> Pad020
  Length = 10
  Length2 = 100
  Profile = -> Sketch061
  Type = 0
FEATURE [PartDesign::Pad] Pad018
  BaseFeature = -> Pocket030
  Direction = (0,0,-1)
  Length = 10
  Length2 = 100
  Profile = -> Sketch060
  Type = 2
  UseCustomVector = true
FEATURE [Sketcher::SketchObject] Sketch064
  AttachmentOffset = pos=(0,0,-33.9) rot=(0,0,1;0rad)
  FullyConstrained = true
  MapMode = 5
  Placement = pos=(0,0,-33.9) rot=(0,0,1;0rad)
  Support = -> [XY_Plane031]
  expr: Constraints[10] = <<StepperBodyShape001>>.Constraints.CenterToEdge
  expr: .AttachmentOffset.Base.z = -<<StepperBodyPad001>>.Length
  sketch-geometry (4):
    g0: LineSegment StartX=-8.1 StartY=25 StartZ=0 EndX=8.1 EndY=25 EndZ=0
    g1: LineSegment StartX=8.1 StartY=25 StartZ=0 EndX=8.1 EndY=21 EndZ=0
    g2: LineSegment StartX=8.1 StartY=21 StartZ=0 EndX=-8.1 EndY=21 EndZ=0
    g3: LineSegment StartX=-8.1 StartY=21 StartZ=0 EndX=-8.1 EndY=25 EndZ=0
  constraints (11):
    c: Coincident(g0,g1)
    c: Coincident(g1,g2)
    c: Coincident(g2,g3)
    c: Coincident(g3,g0)
    c: Horizontal(g2)
    c: Vertical(g1)
    c: Vertical(g3)
    c: DistanceX(g0,g0) = 16.2
    c: Symmetric(g0,g0,g-2)
    c: DistanceY(g3,g3) = 4
    c: DistanceY(g-1,g2) = 21
FEATURE [PartDesign::Pad] Pad021
  BaseFeature = -> Pad018
  Direction = (0,0,1)
  Length = 10.25
  Length2 = 100
  Profile = -> Sketch064
  Type = 0
FEATURE [PartDesign::Body] Body021  label="Stepper34"
  Group = -> [Sketch059,Pad017,Sketch060,Sketch061,Sketch063,Pad020,Pocket030,Pad018,Sketch064,Pad021]
  Origin = -> Origin031
  Tip = -> Pad021
COMPONENT P11 — recipe-attached ("LaserModule", modeled in this document).
Construction recipe (the document's own serialized feature program — sketch geometry with constraints, then the solid features built on it; lengths are millimeters unless a unit is written):

FEATURE [Sketcher::SketchObject] Sketch070
  FullyConstrained = true
  MapMode = 5
  Support = -> [XY_Plane035]
  sketch-geometry (4):
    g0: LineSegment StartX=-20.1 StartY=20.2 StartZ=0 EndX=20.1 EndY=20.2 EndZ=0
    g1: LineSegment StartX=20.1 StartY=20.2 StartZ=0 EndX=20.1 EndY=-20.2 EndZ=0
    g2: LineSegment StartX=20.1 StartY=-20.2 StartZ=0 EndX=-20.1 EndY=-20.2 EndZ=0
    g3: LineSegment StartX=-20.1 StartY=-20.2 StartZ=0 EndX=-20.1 EndY=20.2 EndZ=0
  constraints (11):
    c: Coincident(g0,g1)
    c: Coincident(g1,g2)
    c: Coincident(g2,g3)
    c: Coincident(g3,g0)
    c: Horizontal(g0)
    c: Horizontal(g2)
    c: Vertical(g1)
    c: Vertical(g3)
    c: Symmetric(g1,g0,g-1)
    c: DistanceX(g0,g0) = 40.2
    c: DistanceY(g3,g3) = 40.4
FEATURE [PartDesign::Pad] Pad024
  Direction = (0,0,1)
  Length = 65
  Length2 = 100
  Profile = -> Sketch070
  Type = 0
FEATURE [Sketcher::SketchObject] Sketch071
  AttachmentOffset = pos=(0,0,20.2) rot=(0,0,1;0rad)
  FullyConstrained = true
  MapMode = 5
  Placement = pos=(0,-20.2,-4.5e-15) rot=(1,0,0;1.5708rad)
  Support = -> [XZ_Plane035]
  expr: .AttachmentOffset.Base.z = 20.2
  sketch-geometry (6):
    g0: Circle CenterX=8 CenterY=9 CenterZ=0 NormalX=0 NormalY=0 NormalZ=1 AngleXU=0 Radius=1.3
    g1: Circle CenterX=-8 CenterY=9 CenterZ=0 NormalX=0 NormalY=0 NormalZ=1 AngleXU=0 Radius=1.3
    g2: LineSegment StartX=-6.7 StartY=9 StartZ=0 EndX=6.7 EndY=9 EndZ=0
    g3: LineSegment StartX=9.3 StartY=9 StartZ=0 EndX=20.1 EndY=9 EndZ=0
    g4: Circle CenterX=-8 CenterY=49 CenterZ=0 NormalX=0 NormalY=0 NormalZ=1 AngleXU=0 Radius=1.3
    g5: Circle CenterX=8 CenterY=49 CenterZ=0 NormalX=0 NormalY=0 NormalZ=1 AngleXU=0 Radius=1.3
  constraints (20):
    c: Symmetric(g1,g0,g-2)
    c: Equal(g1,g0)
    c: PointOnObject(g2,g1)
    c: PointOnObject(g2,g0)
    c: Horizontal(g2)
    c: PointOnObject(g0,g2)
    c: Diameter(g1) = 2.6
    c: DistanceX(g2,g2) = 13.4
    c: PointOnObject(g3,g0)
    c: Horizontal(g3)
    c: DistanceX(g3) = 20.1
    c: DistanceX(g3,g3) = 10.8
    c: PointOnObject(g0,g3)
    c: DistanceY(g0) = 9
    c: DistanceY(g4) = 49
    c: Horizontal(g5,g4)
    c: Vertical(g4,g1)
    c: Vertical(g5,g0)
    c: Equal(g4,g5)
    c: Equal(g5,g1)
FEATURE [PartDesign::Pocket] Pocket037
  BaseFeature = -> Pad024
  Length = 5
  Length2 = 100
  Profile = -> Sketch071
  Type = 0
FEATURE [Sketcher::SketchObject] Sketch072
  AttachmentOffset = pos=(0,0,65) rot=(0,0,1;0rad)
  FullyConstrained = true
  MapMode = 5
  Placement = pos=(0,0,65) rot=(0,0,1;0rad)
  Support = -> [XY_Plane035]
  expr: .AttachmentOffset.Base.z = Pad024.Length
  sketch-geometry (8):
    g0: LineSegment StartX=-17.75 StartY=20.35 StartZ=0 EndX=17.75 EndY=20.35 EndZ=0
    g1: LineSegment StartX=20.35 StartY=17.75 StartZ=0 EndX=20.35 EndY=-17.75 EndZ=0
    g2: LineSegment StartX=17.75 StartY=-20.35 StartZ=0 EndX=-17.75 EndY=-20.35 EndZ=0
    g3: LineSegment StartX=-20.35 StartY=-17.75 StartZ=0 EndX=-20.35 EndY=17.75 EndZ=0
    g4: ArcOfCircle CenterX=-17.75 CenterY=17.75 CenterZ=0 NormalX=0 NormalY=0 NormalZ=1 AngleXU=0 Radius=2.6 StartAngle=1.5708 EndAngle=3.14159
    g5: ArcOfCircle CenterX=17.75 CenterY=17.75 CenterZ=0 NormalX=0 NormalY=0 NormalZ=1 AngleXU=0 Radius=2.6 StartAngle=5.07e-14 EndAngle=1.5708
    g6: ArcOfCircle CenterX=17.75 CenterY=-17.75 CenterZ=0 NormalX=0 NormalY=0 NormalZ=1 AngleXU=0 Radius=2.6 StartAngle=4.71239 EndAngle=6.28319
    g7: ArcOfCircle CenterX=-17.75 CenterY=-17.75 CenterZ=0 NormalX=0 NormalY=0 NormalZ=1 AngleXU=0 Radius=2.6 StartAngle=3.14159 EndAngle=4.71239
  constraints (19):
    c: Horizontal(g0)
    c: Horizontal(g2)
    c: Vertical(g1)
    c: Vertical(g3)
    c: Tangent(g3,g4) = 1.5708
    c: Tangent(g0,g4) = 1.5708
    c: Tangent(g0,g5) = 1.5708
    c: Tangent(g1,g5) = 1.5708
    c: Tangent(g1,g6) = 1.5708
    c: Tangent(g2,g6) = 1.5708
    c: Tangent(g2,g7) = 1.5708
    c: Tangent(g3,g7) = 1.5708
    c: DistanceY(g2,g0) = 40.7
    c: DistanceX(g3,g1) = 40.7
    c: Symmetric(g4,g6,g-1)
    c: Equal(g5,g4)
    c: Equal(g4,g7)
    c: Equal(g7,g6)
    c: Radius(g5) = 2.6
FEATURE [PartDesign::Pad] Pad025
  BaseFeature = -> Pocket037
  Direction = (0,0,1)
  Length = 33.5
  Length2 = 100
  Profile = -> Sketch072
  Type = 0
FEATURE [Sketcher::SketchObject] Sketch073
  FullyConstrained = true
  MapMode = 5
  Support = -> [XY_Plane035]
  sketch-geometry (1):
    g0: Circle CenterX=0 CenterY=0 CenterZ=0 NormalX=0 NormalY=0 NormalZ=1 AngleXU=0 Radius=9.05
  constraints (2):
    c: Coincident(g0,g-1)
    c: Diameter(g0) = 18.1
FEATURE [PartDesign::Pad] Pad026
  BaseFeature = -> Pad025
  Direction = (0,0,1)
  Length = 11.66
  Length2 = 100
  Profile = -> Sketch073
  Reversed = true
  Type = 0
FEATURE [Sketcher::SketchObject] Sketch074
  AttachmentOffset = pos=(0,0,98.5) rot=(0,0,1;0rad)
  FullyConstrained = true
  MapMode = 5
  Placement = pos=(0,0,98.5) rot=(0,0,1;0rad)
  Support = -> [XY_Plane035]
  expr: .AttachmentOffset.Base.z = Pad024.Length + Pad025.Length
  sketch-geometry (8):
    g0: Circle CenterX=-16 CenterY=16 CenterZ=0 NormalX=0 NormalY=0 NormalZ=1 AngleXU=0 Radius=2.71
    g1: Circle CenterX=16 CenterY=16 CenterZ=0 NormalX=0 NormalY=0 NormalZ=1 AngleXU=0 Radius=2.71
    g2: Circle CenterX=16 CenterY=-16 CenterZ=0 NormalX=0 NormalY=0 NormalZ=1 AngleXU=0 Radius=2.71
    g3: Circle CenterX=-16 CenterY=-16 CenterZ=0 NormalX=0 NormalY=0 NormalZ=1 AngleXU=0 Radius=2.71
    g4: LineSegment StartX=-16 StartY=16 StartZ=0 EndX=-16 EndY=-16 EndZ=0
    g5: LineSegment StartX=-16 StartY=-16 StartZ=0 EndX=16 EndY=-16 EndZ=0
    g6: LineSegment StartX=16 StartY=-16 StartZ=0 EndX=16 EndY=16 EndZ=0
    g7: LineSegment StartX=16 StartY=16 StartZ=0 EndX=-16 EndY=16 EndZ=0
  constraints (19):
    c: Symmetric(g0,g2,g-1)
    c: Coincident(g4,g0)
    c: Coincident(g4,g3)
    c: Vertical(g4)
    c: Coincident(g5,g3)
    c: Coincident(g5,g2)
    c: Horizontal(g5)
    c: Coincident(g6,g2)
    c: Coincident(g6,g1)
    c: Vertical(g6)
    c: Coincident(g7,g1)
    c: Coincident(g7,g0)
    c: Horizontal(g7)
    c: DistanceX(g7,g7) = 32
    c: Equal(g7,g4)
    c: Diameter(g0) = 5.42
    c: Equal(g0,g1)
    c: Equal(g1,g2)
    c: Equal(g2,g3)
FEATURE [PartDesign::Pad] Pad027
  BaseFeature = -> Pad026
  Direction = (0,0,1)
  Length = 2.85
  Length2 = 100
  Profile = -> Sketch074
  Type = 0
FEATURE [PartDesign::Body] Body023  label="LaserModule"
  Group = -> [Sketch070,Pad024,Sketch071,Pocket037,Sketch072,Pad025,Sketch073,Pad026,Sketch074,Pad027]
  Origin = -> Origin035
  Tip = -> Pad027
COMPONENT P12 — recipe-attached ("BoltM5_16", modeled in this document).
Construction recipe (the document's own serialized feature program — sketch geometry with constraints, then the solid features built on it; lengths are millimeters unless a unit is written):

FEATURE [Sketcher::SketchObject] Sketch077
  FullyConstrained = true
  MapMode = 5
  sketch-geometry (6):
    g0: LineSegment StartX=4.17 StartY=5 StartZ=0 EndX=4.17 EndY=0 EndZ=0
    g1: LineSegment StartX=4.17 StartY=0 StartZ=0 EndX=2.45 EndY=0 EndZ=0
    g2: LineSegment StartX=2.45 StartY=0 StartZ=0 EndX=2.45 EndY=-16 EndZ=0
    g3: LineSegment StartX=2.45 StartY=-16 StartZ=0 EndX=0 EndY=-16 EndZ=0
    g4: LineSegment StartX=4.17 StartY=5 StartZ=0 EndX=0 EndY=5 EndZ=0
    g5: LineSegment StartX=0 StartY=5 StartZ=0 EndX=0 EndY=-16 EndZ=0
  constraints (18):
    c: Coincident(g0,g1)
    c: Horizontal(g1)
    c: Vertical(g0)
    c: PointOnObject(g0,g-1)
    c: Coincident(g2,g3)
    c: Horizontal(g3)
    c: Vertical(g2)
    c: Coincident(g2,g1)
    c: PointOnObject(g3,g-2)
    c: Coincident(g4,g0)
    c: PointOnObject(g4,g-2)
    c: Horizontal(g4)
    c: Coincident(g5,g4)
    c: Coincident(g5,g3)
    c: DistanceX(g4,g4) = 4.17
    c: DistanceY(g0,g0) = 5
    c: DistanceY(g2,g2) = 16
    c: DistanceX(g3,g3) = 2.45
FEATURE [PartDesign::Revolution] Revolution008
  Angle = 360
  Axis = (0,1,0)
  Base = (0,0,0)
  Profile = -> Sketch077
  ReferenceAxis = -> Sketch077 [V_Axis]
FEATURE [PartDesign::Body] Body024  label="BoltM5_16"
  Group = -> [Sketch077,Revolution008]
  Origin = -> Origin037
  Tip = -> Revolution008
COMPONENT P13 — recipe-attached ("BoltM5_12", modeled in this document).
Construction recipe (the document's own serialized feature program — sketch geometry with constraints, then the solid features built on it; lengths are millimeters unless a unit is written):

FEATURE [Sketcher::SketchObject] Sketch078
  FullyConstrained = true
  MapMode = 5
  sketch-geometry (6):
    g0: LineSegment StartX=4.17 StartY=5 StartZ=0 EndX=4.17 EndY=0 EndZ=0
    g1: LineSegment StartX=4.17 StartY=0 StartZ=0 EndX=2.45 EndY=0 EndZ=0
    g2: LineSegment StartX=2.45 StartY=0 StartZ=0 EndX=2.45 EndY=-11.8 EndZ=0
    g3: LineSegment StartX=2.45 StartY=-11.8 StartZ=0 EndX=0 EndY=-11.8 EndZ=0
    g4: LineSegment StartX=4.17 StartY=5 StartZ=0 EndX=0 EndY=5 EndZ=0
    g5: LineSegment StartX=0 StartY=5 StartZ=0 EndX=0 EndY=-11.8 EndZ=0
  constraints (18):
    c: Coincident(g0,g1)
    c: Horizontal(g1)
    c: Vertical(g0)
    c: PointOnObject(g0,g-1)
    c: Coincident(g2,g3)
    c: Horizontal(g3)
    c: Vertical(g2)
    c: Coincident(g2,g1)
    c: PointOnObject(g3,g-2)
    c: Coincident(g4,g0)
    c: PointOnObject(g4,g-2)
    c: Horizontal(g4)
    c: Coincident(g5,g4)
    c: Coincident(g5,g3)
    c: DistanceX(g4,g4) = 4.17
    c: DistanceY(g0,g0) = 5
    c: DistanceY(g2,g2) = 11.8
    c: DistanceX(g3,g3) = 2.45
FEATURE [PartDesign::Revolution] Revolution009
  Angle = 360
  Axis = (0,1,0)
  Base = (0,0,0)
  Profile = -> Sketch078
  ReferenceAxis = -> Sketch078 [V_Axis]
FEATURE [PartDesign::Body] Body025  label="BoltM5_12"
  Group = -> [Sketch078,Revolution009]
  Origin = -> Origin038
  Tip = -> Revolution009
COMPONENT P14 — recipe-attached ("VBearingBushing", modeled in this document).
Construction recipe (the document's own serialized feature program — sketch geometry with constraints, then the solid features built on it; lengths are millimeters unless a unit is written):

FEATURE [Sketcher::SketchObject] Sketch108  label="VBearingBushingProfile"
  AttachmentOffset = pos=(32,0,30.35) rot=(0,0,1;0rad)
  FullyConstrained = true
  MapMode = 5
  Placement = pos=(32,0,30.35) rot=(0,0,1;0rad)
  Support = -> [XY_Plane046]
  expr: .AttachmentOffset.Base.z = Spreadsheet.VBearingOffset + 20mm
  expr: .AttachmentOffset.Base.x = Spreadsheet.XRailBearingSpacing / 2
  sketch-geometry (4):
    g0: LineSegment StartX=2.5 StartY=1 StartZ=0 EndX=10 EndY=1 EndZ=0
    g1: LineSegment StartX=10 StartY=1 StartZ=0 EndX=4.5 EndY=-4.92 EndZ=0
    g2: LineSegment StartX=4.5 StartY=-4.92 StartZ=0 EndX=2.5 EndY=-4.92 EndZ=0
    g3: LineSegment StartX=2.5 StartY=-4.92 StartZ=0 EndX=2.5 EndY=1 EndZ=0
  constraints (12):
    c: Horizontal(g0)
    c: Coincident(g1,g0)
    c: Coincident(g2,g1)
    c: Horizontal(g2)
    c: Coincident(g3,g2)
    c: Coincident(g3,g0)
    c: Vertical(g3)
    c: DistanceY(g3,g3) = 5.92
    c: DistanceX(g-1,g0) = 2.5
    c: DistanceX(g2,g2) = 2
    c: DistanceX(g0,g0) = 7.5
    c: DistanceY(g-1,g0) = 1
FEATURE [PartDesign::Revolution] Revolution013  label="VBearingBushingRev"
  Angle = 360
  Axis = (0,1,0)
  Base = (32,0,30.35)
  Profile = -> Sketch108
  ReferenceAxis = -> Sketch108 [V_Axis]
  Reversed = true
FEATURE [PartDesign::Body] Body031  label="VBearingBushing"
  Group = -> [Sketch108,Revolution013]
  Origin = -> Origin046
  Tip = -> Revolution013
COMPONENT P15 — recipe-attached ("Foot004", modeled in this document).
Construction recipe (the document's own serialized feature program — sketch geometry with constraints, then the solid features built on it; lengths are millimeters unless a unit is written):

FEATURE [Sketcher::SketchObject] Sketch013  label="BraceProfile001"
  FullyConstrained = true
  MapMode = 5
  Support = -> [XY_Plane012]
  sketch-geometry (25):
    g0: LineSegment StartX=70 StartY=-5.5 StartZ=0 EndX=70 EndY=5.5 EndZ=0
    g1: LineSegment StartX=67.9497 StartY=10.4497 StartZ=0 EndX=10.4497 EndY=67.9497 EndZ=0
    g2: LineSegment StartX=5.5 StartY=70 StartZ=0 EndX=-5.5 EndY=70 EndZ=0
    g3: Circle CenterX=20 CenterY=0 CenterZ=0 NormalX=0 NormalY=0 NormalZ=1 AngleXU=0 Radius=2.62
    g4: Circle CenterX=60 CenterY=0 CenterZ=0 NormalX=0 NormalY=0 NormalZ=1 AngleXU=0 Radius=2.62
    g5: Circle CenterX=0 CenterY=0 CenterZ=0 NormalX=0 NormalY=0 NormalZ=1 AngleXU=0 Radius=2.62
    g6: Circle CenterX=0 CenterY=60 CenterZ=0 NormalX=0 NormalY=0 NormalZ=1 AngleXU=0 Radius=2.62
    g7: LineSegment StartX=10 StartY=100 StartZ=0 EndX=10 EndY=-10 EndZ=0
    g8: LineSegment StartX=10 StartY=-10 StartZ=0 EndX=-10 EndY=-10 EndZ=0
    g9: LineSegment StartX=-10 StartY=-10 StartZ=0 EndX=-10 EndY=100 EndZ=0
    g10: LineSegment StartX=10 StartY=10 StartZ=0 EndX=160 EndY=10 EndZ=0
    g11: LineSegment StartX=160 StartY=-10 StartZ=0 EndX=10 EndY=-10 EndZ=0
    g12: LineSegment StartX=10 StartY=-10 StartZ=0 EndX=10 EndY=10 EndZ=0
    g13: ArcOfCircle CenterX=-5.5 CenterY=-5.5 CenterZ=0 NormalX=0 NormalY=0 NormalZ=1 AngleXU=0 Radius=7 StartAngle=3.14159 EndAngle=4.71239
    g14: ArcOfCircle CenterX=-5.5 CenterY=63 CenterZ=0 NormalX=0 NormalY=0 NormalZ=1 AngleXU=0 Radius=7 StartAngle=1.5708 EndAngle=3.14159
    g15: ArcOfCircle CenterX=5.5 CenterY=63 CenterZ=0 NormalX=0 NormalY=0 NormalZ=1 AngleXU=0 Radius=7 StartAngle=0.785398 EndAngle=1.5708
    g16: ArcOfCircle CenterX=63 CenterY=5.5 CenterZ=0 NormalX=0 NormalY=0 NormalZ=1 AngleXU=0 Radius=7 StartAngle=0 EndAngle=0.785398
    g17: ArcOfCircle CenterX=63 CenterY=-5.5 CenterZ=0 NormalX=0 NormalY=0 NormalZ=1 AngleXU=0 Radius=7 StartAngle=4.71239 EndAngle=6.28319
    g18: LineSegment StartX=-12.5 StartY=-5.5 StartZ=0 EndX=-12.5 EndY=63 EndZ=0
    g19: LineSegment StartX=-5.5 StartY=-12.5 StartZ=0 EndX=63 EndY=-12.5 EndZ=0
    g20: Circle CenterX=0 CenterY=20 CenterZ=0 NormalX=0 NormalY=0 NormalZ=1 AngleXU=0 Radius=2.62
    g21: LineSegment StartX=0 StartY=0 StartZ=0 EndX=20 EndY=0 EndZ=0
    g22: LineSegment StartX=0 StartY=0 StartZ=0 EndX=0 EndY=20 EndZ=0
    g23: Circle CenterX=24.7487 CenterY=24.7487 CenterZ=0 NormalX=0 NormalY=0 NormalZ=1 AngleXU=0 Radius=2.65
    g24: LineSegment StartX=0 StartY=0 StartZ=0 EndX=24.7487 EndY=24.7487 EndZ=0
  constraints (65):
    c: Vertical(g0)
    c: Horizontal(g2)
    c: PointOnObject(g3,g-1)
    c: PointOnObject(g4,g-1)
    c: PointOnObject(g5,g-2)
    c: PointOnObject(g6,g-2)
    c: Equal(g6,g5)
    c: Equal(g5,g3)
    c: Equal(g3,g4)
    c: Distance(g3,g4) = 40
    c: Distance(g5,g6) = 60
    c: Coincident(g7,g8)
    c: Coincident(g8,g9)
    c: Vertical(g7)
    c: Vertical(g9)
    c: DistanceY(g8,g-1) = 10
    c: DistanceX(g8,g8) = 20
    c: Symmetric(g8,g7,g-2)
    c: DistanceY(g9,g9) = 110
    c: Equal(g7,g9)
    c: Coincident(g11,g12)
    c: Coincident(g12,g10)
    c: Horizontal(g10)
    c: Horizontal(g11)
    c: Vertical(g12)
    c: PointOnObject(g11,g8)
    c: DistanceX(g11,g11) = 150
    c: Equal(g11,g10)
    c: Symmetric(g10,g7,g-1)
    c: DistanceX(g-1,g3) = 20
    c: DistanceY(g-1,g5) = 0
    c: Tangent(g2,g14) = -1.5708
    c: Tangent(g2,g15) = -1.5708
    c: Tangent(g1,g15) = -1.5708
    c: Tangent(g1,g16) = -1.5708
    c: Tangent(g0,g16) = -1.5708
    c: Tangent(g0,g17) = -1.5708
    c: Equal(g16,g13)
    c: Equal(g13,g14)
    c: Radius(g14) = 7
    c: DistanceY(g6,g2) = 10
    c: DistanceX(g4,g0) = 10
    c: Symmetric(g15,g14,g-2)
    c: Symmetric(g16,g17,g-1)
    c: Diameter(g5) = 5.24
    c: Vertical(g18)
    c: DistanceX(g13,g8) = 2.5
    c: Tangent(g18,g13) = 1.5708
    c: Tangent(g18,g14) = 1.5708
    c: Horizontal(g19)
    c: Tangent(g19,g17) = -1.5708
    c: Tangent(g19,g13) = -1.5708
    c: DistanceY(g13,g8) = 2.5
    c: PointOnObject(g20,g-2)
    c: Equal(g20,g5)
    c: Coincident(g21,g5)
    c: Coincident(g21,g3)
    c: Coincident(g22,g5)
    c: Coincident(g22,g20)
    c: Equal(g22,g21)
    c: Diameter(g23) = 5.3
    c: Coincident(g24,g5)
    c: Coincident(g24,g23)
    c: PointOnObject(g10,g24)
    c: Distance(g24) = 35
FEATURE [PartDesign::Pad] Pad006
  Direction = (0,0,1)
  Length = 32
  Length2 = 3
  Profile = -> Sketch013
  Reversed = true
  Type = 4
  expr: Length = Spreadsheet.XRailZClearance
FEATURE [Sketcher::SketchObject] Sketch014  label="CounterSinkHolesBottom"
  AttachmentOffset = pos=(0,0,-32) rot=(0,0,1;0rad)
  ExternalGeometry = -> [Sketch013]
  FullyConstrained = true
  MapMode = 5
  Placement = pos=(0,0,-32) rot=(0,0,1;0rad)
  Support = -> [XY_Plane012]
  expr: .AttachmentOffset.Base.z = -Spreadsheet.XRailZClearance
  sketch-geometry (5):
    g0: Circle CenterX=0 CenterY=60 CenterZ=0 NormalX=0 NormalY=0 NormalZ=1 AngleXU=0 Radius=4.75
    g1: Circle CenterX=0 CenterY=0 CenterZ=0 NormalX=0 NormalY=0 NormalZ=1 AngleXU=0 Radius=4.75
    g2: Circle CenterX=20 CenterY=0 CenterZ=0 NormalX=0 NormalY=0 NormalZ=1 AngleXU=0 Radius=4.75
    g3: Circle CenterX=60 CenterY=0 CenterZ=0 NormalX=0 NormalY=0 NormalZ=1 AngleXU=0 Radius=4.75
    g4: Circle CenterX=0 CenterY=20 CenterZ=0 NormalX=0 NormalY=0 NormalZ=1 AngleXU=0 Radius=4.75
  constraints (10):
    c: Coincident(g0,g-4)
    c: Coincident(g1,g-3)
    c: Coincident(g2,g-5)
    c: Coincident(g3,g-6)
    c: Equal(g3,g2)
    c: Equal(g2,g1)
    c: Equal(g1,g0)
    c: Diameter(g0) = 9.5
    c: Coincident(g4,g-7)
    c: Equal(g4,g0)
FEATURE [PartDesign::Pocket] Pocket004
  BaseFeature = -> Pad006
  Length = 17
  Length2 = 100
  Profile = -> Sketch014
  Reversed = true
  Type = 0
FEATURE [Sketcher::SketchObject] Sketch016  label="BraceProfile002"
  FullyConstrained = true
  MapMode = 5
  Support = -> [XY_Plane012]
  sketch-geometry (6):
    g0: LineSegment StartX=10 StartY=100 StartZ=0 EndX=10 EndY=10 EndZ=0
    g1: LineSegment StartX=-10 StartY=-10 StartZ=0 EndX=-10 EndY=100 EndZ=0
    g2: LineSegment StartX=10 StartY=10 StartZ=0 EndX=140 EndY=10 EndZ=0
    g3: LineSegment StartX=-10 StartY=100 StartZ=0 EndX=10 EndY=100 EndZ=0
    g4: LineSegment StartX=140 StartY=10 StartZ=0 EndX=140 EndY=-10 EndZ=0
    g5: LineSegment StartX=-10 StartY=-10 StartZ=0 EndX=140 EndY=-10 EndZ=0
  constraints (17):
    c: Vertical(g0)
    c: Vertical(g1)
    c: DistanceY(g1,g1) = 110
    c: Horizontal(g2)
    c: Horizontal(g3)
    c: Vertical(g4)
    c: Coincident(g5,g1)
    c: Coincident(g5,g4)
    c: Horizontal(g5)
    c: DistanceX(g3,g3) = 20
    c: Coincident(g0,g3)
    c: Coincident(g0,g2)
    c: DistanceY(g4,g4) = 20
    c: Coincident(g2,g4)
    c: Coincident(g3,g1)
    c: Symmetric(g1,g0,g-1)
    c: DistanceX(g5,g5) = 150
FEATURE [PartDesign::Pocket] Pocket005
  BaseFeature = -> Pocket004
  Length = 5
  Length2 = 100
  Profile = -> Sketch016
  Reversed = true
  Type = 1
FEATURE [Sketcher::SketchObject] Sketch109  label="BraceProfile003"
  ExternalGeometry = -> [Sketch013]
  FullyConstrained = true
  MapMode = 5
  Support = -> [XY_Plane012]
  sketch-geometry (1):
    g0: Circle CenterX=24.7487 CenterY=24.7487 CenterZ=0 NormalX=0 NormalY=0 NormalZ=1 AngleXU=0 Radius=4.75
  constraints (2):
    c: Coincident(g0,g-3)
    c: Diameter(g0) = 9.5
FEATURE [PartDesign::Pocket] Pocket055
  BaseFeature = -> Pocket005
  Length = 22
  Length2 = 100
  Profile = -> Sketch109
  Type = 4
FEATURE [PartDesign::Body] Body007  label="Foot"
  Group = -> [Sketch013,Pad006,Sketch014,Pocket004,Sketch016,Pocket005,Sketch109,Pocket055]
  Origin = -> Origin012
  Tip = -> Pocket055
COMPONENT P16 — same part as P15; its construction recipe is shown at P15.
COMPONENT P17 — geometry summary ("CNC"; no construction recipe available for this part):
  bounding box: 1244.6 x 711.2 x 184.0 mm
  tessellated surface: 60,318 triangles
  volume: 21019067 mm^3 (13% of its bounding box)
PROVENANCE & LICENSES
A FreeCAD (.FCStd) document from a public repository crawl; recipes are the document's own serialized feature recipes (and, for linked parts, companion documents' recipes).
License: as declared in the source repository (recorded in the dataset sidecar).
